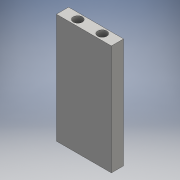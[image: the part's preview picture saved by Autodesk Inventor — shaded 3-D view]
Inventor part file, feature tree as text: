
AUTODESK INVENTOR PART (.ipt)
format: ipt  version: 2016 (Build 200138000, 138)  size: 98,816 bytes
history: native  units: mm
features: extrude x2, sketch x2
ambient origin geometry x8: Origin, YZ Plane, XZ Plane, XY Plane, X Axis, Y Axis, Z Axis, Center Point
bodies: Solid1 (feature_tree)
feature tree (4):
  extrude  "Extrusion1"  Depth=90.0mm
  extrude  "Extrusion2"  Depth=20.0mm
  sketch  "Sketch1"  dims[d0=180.0mm d1=90.0mm]
  sketch  "Sketch2"  dims[d2=20.0mm d3=0.0mm d4=20.0mm d5=20.0mm d6=10.0mm d7=10.0mm d8=15.0mm d9=15.0mm d10=20.0mm d11=0.0mm]
